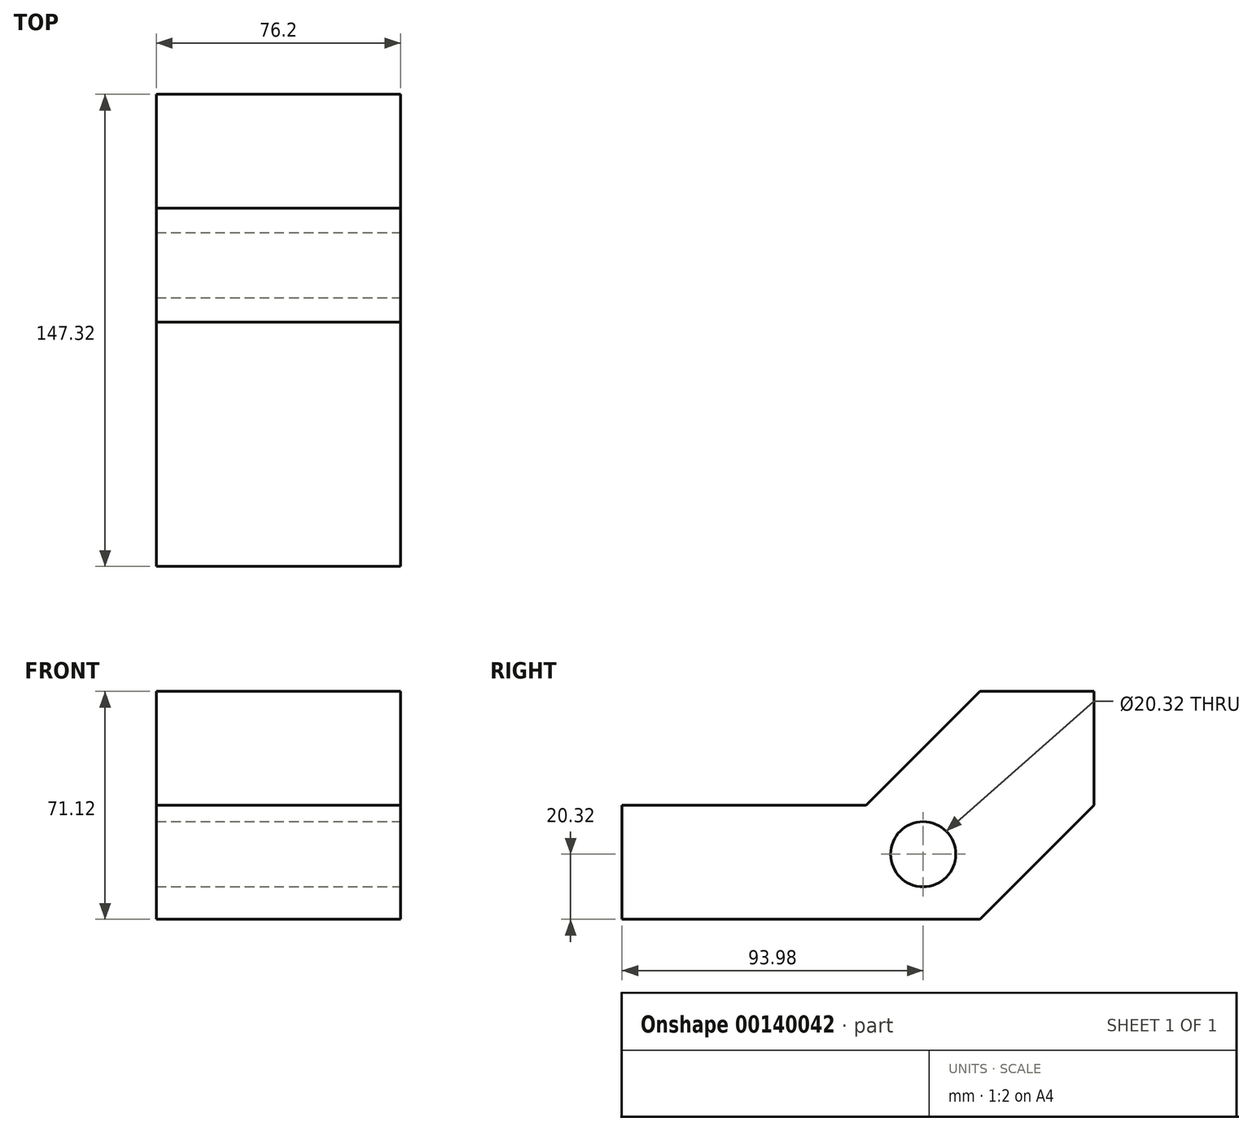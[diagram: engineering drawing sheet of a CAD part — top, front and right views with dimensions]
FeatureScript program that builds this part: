
annotation { "Feature Type Name" : "Feature", "Feature Type Description" : "" }
export const myFeature = defineFeature(function(context is Context, id is Id, definition is map)
    precondition{}
    {
        {
            var Q0;
            Q0=qCreatedBy(makeId("Right.planeOp"),FACE);
            var sketch = newSketch(context, id + "F0", { "sketchPlane" : qUnion([Q0])});
            skLineSegment(sketch, "E0", {"start": v(-111.76, 35.56) * mm, "end": v(-111.76, 0) * mm});
            skLineSegment(sketch, "E1", {"start": v(-111.76, 0) * mm, "end": v(0, 0) * mm});
            skLineSegment(sketch, "E2", {"start": v(0, 0) * mm, "end": v(35.56, 35.56) * mm});
            skLineSegment(sketch, "E3", {"start": v(35.56, 35.56) * mm, "end": v(35.56, 71.12) * mm});
            skLineSegment(sketch, "E4", {"start": v(35.56, 71.12) * mm, "end": v(0, 71.12) * mm});
            skLineSegment(sketch, "E5", {"start": v(0, 71.12) * mm, "end": v(-35.56, 35.56) * mm});
            skLineSegment(sketch, "E6", {"start": v(-35.56, 35.56) * mm, "end": v(-111.76, 35.56) * mm});
            skCircle(sketch, "E7", {"center": v(-17.78, 20.32) * mm, "radius": 10.16 * mm});
            skSolve(sketch);
        }
        {
            var Q0;
            Q0=makeQuery(id+"F0.imprint","IMPRINT",FACE,{"disambiguationData":[TD([[makeQuery(id+"F0.imprint","IMPRINT",EDGE,{"derivedFrom":sQuery(id+"F0.wireOp",EDGE,"E0")}),1.0]])]});
            extrude(context, id + "F1", {"entities" : qUnion([Q0]), "oppositeDirection" : true, "depth" : 76.2 * mm});
        }
    });
